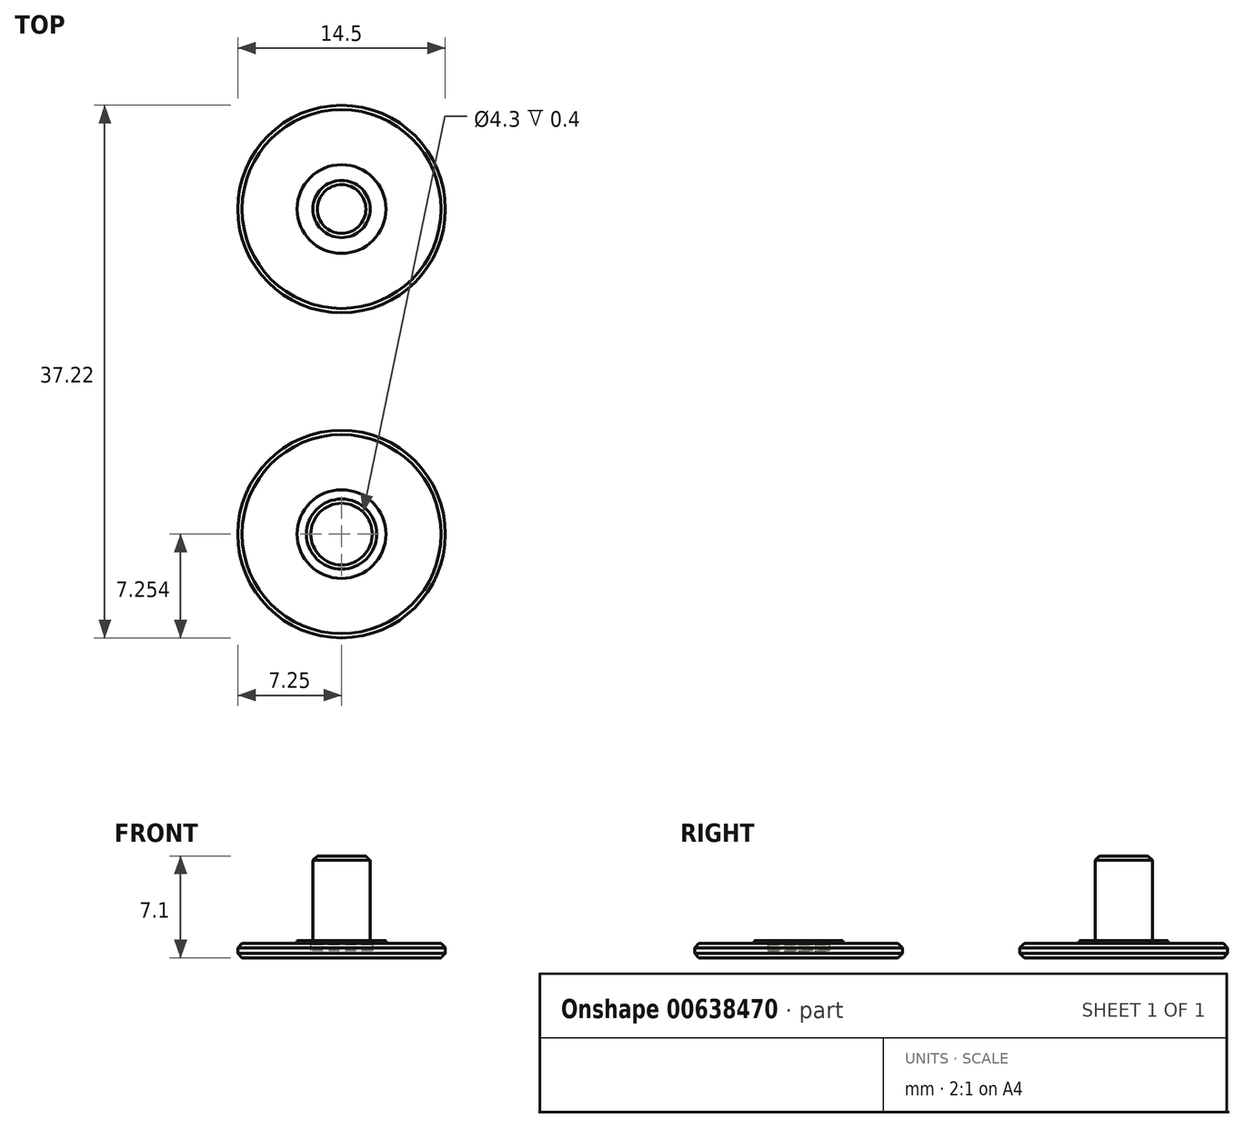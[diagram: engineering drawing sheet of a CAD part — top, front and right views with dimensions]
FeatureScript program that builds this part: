
annotation { "Feature Type Name" : "Feature", "Feature Type Description" : "" }
export const myFeature = defineFeature(function(context is Context, id is Id, definition is map)
    precondition{}
    {
        {
            var Q0;
            Q0=qCreatedBy(makeId("Top.planeOp"),FACE);
            var sketch = newSketch(context, id + "F0", { "sketchPlane" : qUnion([Q0])});
            skCircle(sketch, "E0", {"center": v(0, 0) * mm, "radius": 7.25 * mm});
            skCircle(sketch, "E1", {"center": v(0, 0) * mm, "radius": 3.1 * mm});
            skCircle(sketch, "E2", {"center": v(0, 0) * mm, "radius": 2 * mm});
            skCircle(sketch, "E3", {"center": v(0, -22.72) * mm, "radius": 7.25 * mm});
            skCircle(sketch, "E4", {"center": v(0, -22.72) * mm, "radius": 3.1 * mm});
            skCircle(sketch, "E5", {"center": v(0, -22.72) * mm, "radius": 2.15 * mm});
            skSolve(sketch);
        }
        {
            var Q0;
            Q0=makeQuery(id+"F0.imprint","IMPRINT",FACE,{"disambiguationData":[TD([[makeQuery(id+"F0.imprint","IMPRINT",EDGE,{"derivedFrom":sQuery(id+"F0.wireOp",EDGE,"E0")}),1.0]])]});
            var Q1;
            Q1=makeQuery(id+"F0.imprint","IMPRINT",FACE,{"disambiguationData":[TD([[makeQuery(id+"F0.imprint","IMPRINT",EDGE,{"derivedFrom":sQuery(id+"F0.wireOp",EDGE,"E3")}),1.0]])]});
            extrude(context, id + "F1", {"entities" : qUnion([Q0, Q1]), "depth" : 1 * mm, "offsetDistance" : 25 * mm});
        }
        {
            var Q0;
            Q0=makeQuery(id+"F0.imprint","IMPRINT",FACE,{"disambiguationData":[TD([[makeQuery(id+"F0.imprint","IMPRINT",EDGE,{"derivedFrom":sQuery(id+"F0.wireOp",EDGE,"E1")}),1.0]])]});
            var Q1;
            Q1=makeQuery(id+"F0.imprint","IMPRINT",FACE,{"disambiguationData":[TD([[makeQuery(id+"F0.imprint","IMPRINT",EDGE,{"derivedFrom":sQuery(id+"F0.wireOp",EDGE,"E4")}),1.0]])]});
            extrude(context, id + "F2", {"entities" : qUnion([Q0, Q1]), "operationType" : NewBodyOperationType.ADD, "depth" : (1 + 0.2) * mm, "offsetDistance" : 25 * mm});
        }
        {
            var Q0;
            Q0=makeQuery(id+"F0.imprint","IMPRINT",FACE,{"disambiguationData":[TD([[makeQuery(id+"F0.imprint","IMPRINT",EDGE,{"derivedFrom":sQuery(id+"F0.wireOp",EDGE,"E2")}),1.0]])]});
            extrude(context, id + "F3", {"entities" : qUnion([Q0]), "operationType" : NewBodyOperationType.ADD, "depth" : (1 + 0.3 + 5 + 0.8) * mm, "offsetDistance" : 25 * mm});
        }
        {
            var Q0;
            Q0=makeQuery(id+"F0.imprint","IMPRINT",FACE,{"disambiguationData":[TD([[makeQuery(id+"F0.imprint","IMPRINT",EDGE,{"derivedFrom":sQuery(id+"F0.wireOp",EDGE,"E5")}),1.0]])]});
            extrude(context, id + "F4", {"entities" : qUnion([Q0]), "operationType" : NewBodyOperationType.ADD, "depth" : 0.5 * mm, "offsetDistance" : 25 * mm});
        }
        {
            var Q0;
            {var subQ0=sQuery(id+"F0.wireOp",EDGE,"E5");var subQ1=sQuery(id+"F0.wireOp",EDGE,"E4");Q0=makeQuery(id+"F4.boolean.opBoolean","MERGE",FACE,{"derivedFrom":[makeQuery(id+"F2.boolean.opBoolean","MERGE",FACE,{"derivedFrom":[makeQuery(id+"F1.opExtrude","CAP_FACE",FACE,{"disambiguationData":[OSD([sQuery(id+"F0.wireOp",EDGE,"E3"),subQ1])],"isStart":true}),makeQuery(id+"F2.opExtrude","CAP_FACE",FACE,{"disambiguationData":[OSD([subQ1,subQ0])],"isStart":true})]}),makeQuery(id+"F4.opExtrude","CAP_FACE",FACE,{"disambiguationData":[OSD([subQ0])],"isStart":true})]});}
            var Q1;
            {var subQ0=sQuery(id+"F0.wireOp",EDGE,"E2");var subQ1=sQuery(id+"F0.wireOp",EDGE,"E1");Q1=makeQuery(id+"F3.boolean.opBoolean","MERGE",FACE,{"derivedFrom":[makeQuery(id+"F2.boolean.opBoolean","MERGE",FACE,{"derivedFrom":[makeQuery(id+"F1.opExtrude","CAP_FACE",FACE,{"disambiguationData":[OSD([sQuery(id+"F0.wireOp",EDGE,"E0"),subQ1])],"isStart":true}),makeQuery(id+"F2.opExtrude","CAP_FACE",FACE,{"disambiguationData":[OSD([subQ1,subQ0])],"isStart":true})]}),makeQuery(id+"F3.opExtrude","CAP_FACE",FACE,{"disambiguationData":[OSD([subQ0])],"isStart":true})]});}
            var Q2;
            Q2=makeQuery(id+"F1.opExtrude","CAP_EDGE",EDGE,{"disambiguationData":[OSD([sQuery(id+"F0.wireOp",EDGE,"E0")])],"isStart":false});
            var Q3;
            Q3=makeQuery(id+"F1.opExtrude","CAP_EDGE",EDGE,{"disambiguationData":[OSD([sQuery(id+"F0.wireOp",EDGE,"E3")])],"isStart":false});
            var Q4;
            Q4=makeQuery(id+"F1.opExtrude","CAP_EDGE",EDGE,{"disambiguationData":[OSD([sQuery(id+"F0.wireOp",EDGE,"E4")])],"isStart":false});
            var Q5;
            Q5=makeQuery(id+"F1.opExtrude","CAP_EDGE",EDGE,{"disambiguationData":[OSD([sQuery(id+"F0.wireOp",EDGE,"E1")])],"isStart":false});
            var Q6;
            Q6=makeQuery(id+"F2.opExtrude","CAP_EDGE",EDGE,{"disambiguationData":[OSD([sQuery(id+"F0.wireOp",EDGE,"E5")])],"isStart":false});
            var Q7;
            Q7=makeQuery(id+"F3.opExtrude","CAP_EDGE",EDGE,{"disambiguationData":[OSD([sQuery(id+"F0.wireOp",EDGE,"E2")])],"isStart":false});
            chamfer(context, id + "F5", {"entities" : qUnion([Q0, Q1, Q2, Q3, Q4, Q5, Q6, Q7]), "width" : 0.3 * mm, "tangentPropagation" : true});
        }
    });
